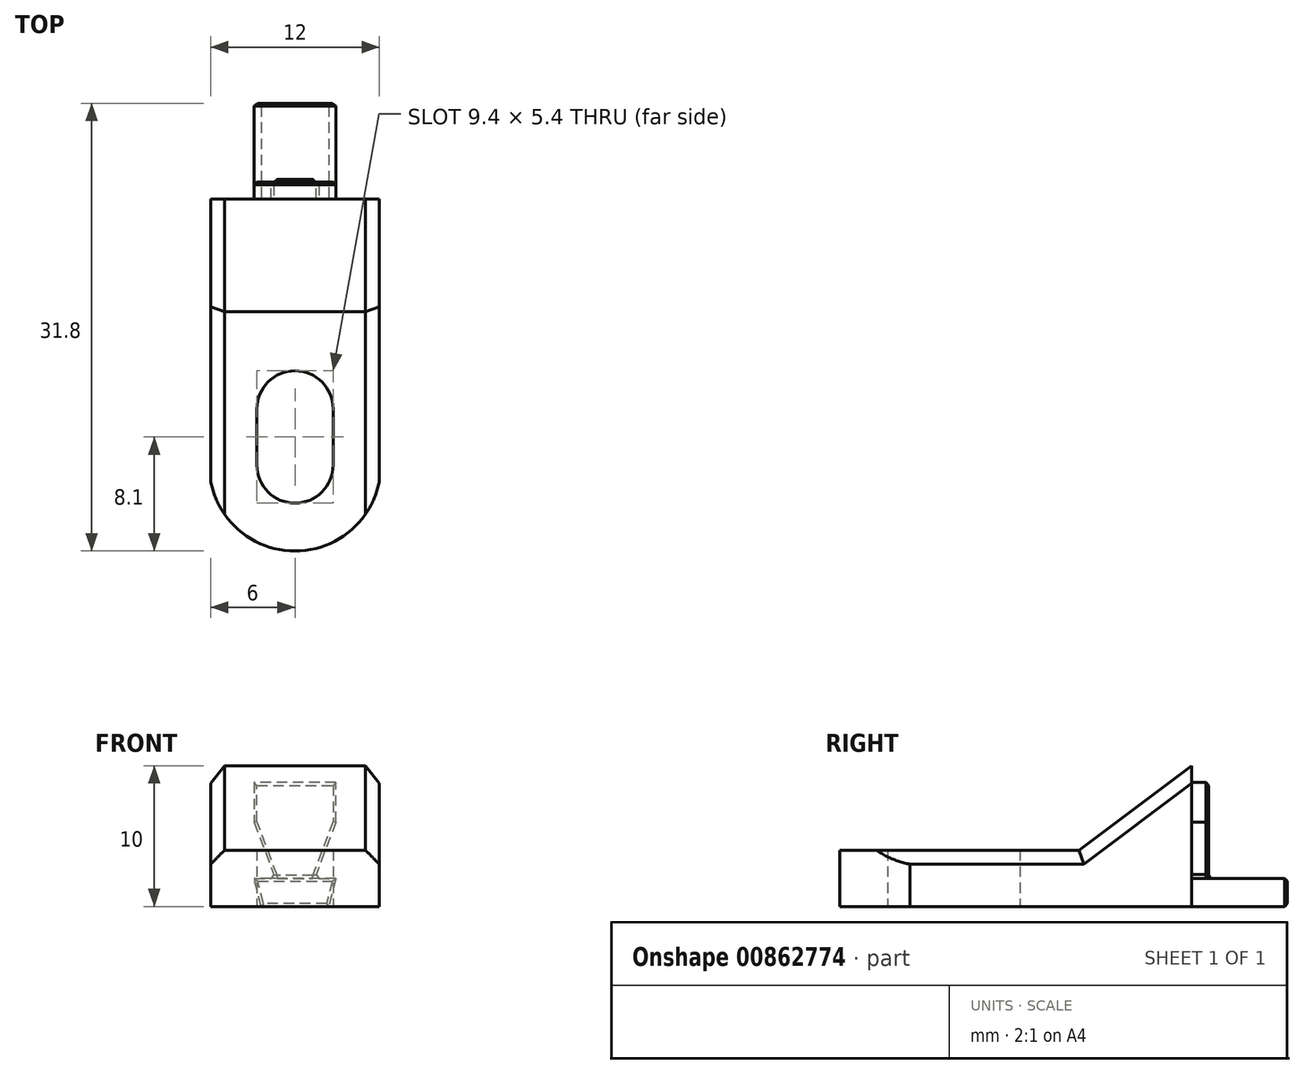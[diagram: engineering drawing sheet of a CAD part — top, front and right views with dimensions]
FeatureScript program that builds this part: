
annotation { "Feature Type Name" : "Feature", "Feature Type Description" : "" }
export const myFeature = defineFeature(function(context is Context, id is Id, definition is map)
    precondition{}
    {
        {
            var Q0;
            Q0=qCreatedBy(makeId("Right.planeOp"),FACE);
            var sketch = newSketch(context, id + "F0", { "sketchPlane" : qUnion([Q0])});
            skLineSegment(sketch, "E0", {"start": v(-25, 0) * mm, "end": v(-25, 4) * mm});
            skLineSegment(sketch, "E1", {"start": v(-25, 4) * mm, "end": v(-8, 4) * mm});
            skLineSegment(sketch, "E2", {"start": v(-8, 4) * mm, "end": v(0, 10) * mm});
            skLineSegment(sketch, "E3", {"start": v(0, 10) * mm, "end": v(0, 0) * mm});
            skLineSegment(sketch, "E4", {"start": v(0, 0) * mm, "end": v(-25, 0) * mm});
            skSolve(sketch);
        }
        {
            var Q0;
            Q0 = qSketchRegion(id + "F0", true);
            extrude(context, id + "F1", {"entities" : qUnion([Q0]), "depth" : 12 * mm, "offsetDistance" : 25 * mm});
        }
        {
            var Q0;
            Q0=makeQuery(id+"F1.opExtrude","SWEPT_FACE",FACE,{"disambiguationData":[OSD([sQuery(id+"F0.wireOp",EDGE,"E3")])]});
            var sketch = newSketch(context, id + "F2", { "sketchPlane" : qUnion([Q0])});
            skLineSegment(sketch, "E5", {"start": v(-8.4, 0) * mm, "end": v(-3.6, 0) * mm});
            skLineSegment(sketch, "E6", {"start": v(-3.6, 0) * mm, "end": v(-3.1, 2) * mm});
            skLineSegment(sketch, "E7", {"start": v(-3.1, 2) * mm, "end": v(-8.9, 2) * mm});
            skLineSegment(sketch, "E8", {"start": v(-8.9, 2) * mm, "end": v(-8.4, 0) * mm});
            skLineSegment(sketch, "E9", {"start": v(-6, 10) * mm, "end": v(-6, 0) * mm, "construction": true});
            skSolve(sketch);
        }
        {
            var Q0;
            Q0 = qSketchRegion(id + "F2", true);
            extrude(context, id + "F3", {"entities" : qUnion([Q0]), "operationType" : NewBodyOperationType.ADD, "depth" : 6.8 * mm, "offsetDistance" : 25 * mm});
        }
        {
            var Q0;
            Q0=makeQuery(id+"F3.boolean.opBoolean","MERGE",FACE,{"derivedFrom":[makeQuery(id+"F1.opExtrude","SWEPT_FACE",FACE,{"disambiguationData":[OSD([sQuery(id+"F0.wireOp",EDGE,"E4")])]}),makeQuery(id+"F3.opExtrude","SWEPT_FACE",FACE,{"disambiguationData":[OSD([sQuery(id+"F2.wireOp",EDGE,"E5")])]})]});
            var sketch = newSketch(context, id + "F4", { "sketchPlane" : qUnion([Q0])});
            skLineSegment(sketch, "E10", {"start": v(6, 25) * mm, "end": v(6, -6.8) * mm, "construction": true});
            skArc(sketch, "E11", {"start": v(12, 20) * mm, "mid": v(6, 25) * mm, "end": v(0, 20) * mm});
            skLineSegment(sketch, "E12", {"start": v(12, 20) * mm, "end": v(12, 25) * mm});
            skLineSegment(sketch, "E13", {"start": v(12, 25) * mm, "end": v(0, 25) * mm});
            skLineSegment(sketch, "E14", {"start": v(0, 25) * mm, "end": v(0, 20) * mm});
            skArc(sketch, "E15", {"start": v(8.7, 18.9) * mm, "mid": v(6, 21.6) * mm, "end": v(3.3, 18.9) * mm});
            skArc(sketch, "E16", {"start": v(3.3, 14.9) * mm, "mid": v(6, 12.2) * mm, "end": v(8.7, 14.9) * mm});
            skLineSegment(sketch, "E17", {"start": v(0, 14.9) * mm, "end": v(12, 14.9) * mm, "construction": true});
            skLineSegment(sketch, "E18", {"start": v(3.3, 14.9) * mm, "end": v(3.3, 18.9) * mm});
            skLineSegment(sketch, "E19", {"start": v(8.7, 14.9) * mm, "end": v(8.7, 18.9) * mm});
            skSolve(sketch);
        }
        {
            var Q0;
            Q0 = qSketchRegion(id + "F4", true);
            var Q1;
            Q1=makeQuery(id+"F1.opExtrude","SWEPT_FACE",FACE,{"disambiguationData":[OSD([sQuery(id+"F0.wireOp",EDGE,"E1")])]});
            extrude(context, id + "F5", {"entities" : qUnion([Q0]), "operationType" : NewBodyOperationType.REMOVE, "endBound" : BoundingType.UP_TO_SURFACE, "oppositeDirection" : true, "depth" : 25 * mm, "endBoundEntityFace" : qUnion([Q1]), "offsetDistance" : 25 * mm});
        }
        {
            var Q0;
            Q0=makeQuery(id+"F1.opExtrude","CAP_EDGE",EDGE,{"disambiguationData":[OSD([sQuery(id+"F0.wireOp",EDGE,"E2")])],"isStart":true});
            var Q1;
            Q1=makeQuery(id+"F1.opExtrude","CAP_EDGE",EDGE,{"disambiguationData":[OSD([sQuery(id+"F0.wireOp",EDGE,"E1")])],"isStart":true});
            var Q2;
            Q2=makeQuery(id+"F1.opExtrude","CAP_EDGE",EDGE,{"disambiguationData":[OSD([sQuery(id+"F0.wireOp",EDGE,"E2")])],"isStart":false});
            var Q3;
            Q3=makeQuery(id+"F1.opExtrude","CAP_EDGE",EDGE,{"disambiguationData":[OSD([sQuery(id+"F0.wireOp",EDGE,"E1")])],"isStart":false});
            var Q4;
            {var subQ0=sQuery(id+"F4.wireOp",EDGE,"E11");var subQ2=makeQuery(id+"F4.imprint","INTERSECT",VERTEX,{"derivedFrom":[subQ0,sQuery(id+"F4.wireOp",EDGE,"E13")]});var subQ3=makeQuery(id+"F1.opExtrude","SWEPT_FACE",FACE,{"disambiguationData":[OSD([sQuery(id+"F0.wireOp",EDGE,"E1")])]});Q4=makeQuery(id+"F5.boolean.opBoolean","TWEAK_EDGE",EDGE,{"derivedFrom":[makeQuery(id+"F5.opExtrude","TWEAK_EDGE",EDGE,{"derivedFrom":[subQ3,makeQuery(id+"F4.imprint","IMPRINT",EDGE,{"disambiguationData":[TD([[subQ2,1.0]])],"derivedFrom":subQ0})]}),makeQuery(id+"F5.opExtrude","TWEAK_EDGE",EDGE,{"derivedFrom":[subQ3,makeQuery(id+"F4.imprint","IMPRINT",EDGE,{"disambiguationData":[TD([[subQ2,-1.0]])],"derivedFrom":subQ0})]})]});}
            chamfer(context, id + "F6", {"entities" : qUnion([Q0, Q1, Q2, Q3, Q4]), "width" : 1 * mm, "tangentPropagation" : true});
        }
        {
            var Q0;
            Q0=makeQuery(id+"F1.opExtrude","SWEPT_FACE",FACE,{"disambiguationData":[OSD([sQuery(id+"F0.wireOp",EDGE,"E3")])]});
            var sketch = newSketch(context, id + "F7", { "sketchPlane" : qUnion([Q0])});
            skLineSegment(sketch, "E20.bottom", {"start": v(-7.4, 2) * mm, "end": v(-4.6, 2) * mm});
            skLineSegment(sketch, "E21", {"start": v(-8.9, 6) * mm, "end": v(-8.9, 8.8) * mm});
            skLineSegment(sketch, "E22", {"start": v(-8.9, 8.8) * mm, "end": v(-3.1, 8.8) * mm});
            skLineSegment(sketch, "E23", {"start": v(-3.1, 8.8) * mm, "end": v(-3.1, 6) * mm});
            skLineSegment(sketch, "E24", {"start": v(-8.9, 6) * mm, "end": v(-7.4, 2) * mm});
            skLineSegment(sketch, "E25", {"start": v(-3.1, 6) * mm, "end": v(-4.6, 2) * mm});
            skSolve(sketch);
        }
        {
            var Q0;
            Q0 = qSketchRegion(id + "F7", true);
            extrude(context, id + "F8", {"entities" : qUnion([Q0]), "operationType" : NewBodyOperationType.ADD, "depth" : 1.2 * mm, "offsetDistance" : 25 * mm});
        }
        {
            var Q0;
            Q0=makeQuery(id+"F8.opExtrude","CAP_FACE",FACE,{"disambiguationData":[OSD([sQuery(id+"F7.wireOp",EDGE,"E20.bottom"),sQuery(id+"F7.wireOp",EDGE,"E20.left"),sQuery(id+"F7.wireOp",EDGE,"E20.right"),sQuery(id+"F7.wireOp",EDGE,"0vDqrzez-4jqf-WyZf-85Mw-JtrNAiH4M5J7"),sQuery(id+"F7.wireOp",EDGE,"E21"),sQuery(id+"F7.wireOp",EDGE,"E22"),sQuery(id+"F7.wireOp",EDGE,"E23"),sQuery(id+"F7.wireOp",EDGE,"Zq4ew7pF-JLNJ-Rp7U-Ze5C-4Ze5DH7dicMg")])],"isStart":false});
            var Q1;
            Q1=makeQuery(id+"F3.opExtrude","CAP_FACE",FACE,{"disambiguationData":[OSD([sQuery(id+"F2.wireOp",EDGE,"E5"),sQuery(id+"F2.wireOp",EDGE,"E6"),sQuery(id+"F2.wireOp",EDGE,"E7"),sQuery(id+"F2.wireOp",EDGE,"E8")])],"isStart":false});
            chamfer(context, id + "F9", {"entities" : qUnion([Q0, Q1]), "width" : .2 * mm, "tangentPropagation" : true});
        }
    });
